# Revit family: Cortadora_CA-31_1_GENERADO
name_source: partatom
category: Equipos especializados
revit_build: Autodesk Revit 2014 (Build: 20131024_2115(x64)
units: mm (PartAtom-declared; Revit-internal decimal feet)

## types (7) — shared parameters
Depth = 405 mm  [stored 1.32874 ft]
Fabricante = SAMMIC S.L.
Foodservice Equipment Identifier = Sí
Height = 544 mm  [stored 1.78478 ft]
Revision Code = 1
Specification by Manufacturer = Single-speed motor block + Regular hopper.
URL = https://www.sammic.com
URL Cutsheet = http://www.sammic.com
Weight in Pounds = 46.3
Width = 389 mm  [stored 1.27625 ft]

## per-type parameters (varying)
| type | Comentarios de tipo | Cycle | Electric Connection Type | FL Amps | Modelo | Phase | Volts |
| Vegetable preparation machine CA-31 230-400/50/3N | Vegetable preparation machine. Production up to 450 kg/hour.

ELECTRICAL DATA:

230V/50Hz/3~ (2.1A) | 50 Hz |  | 1 A | 1050701 | 3 | 400 V |
| Vegetable preparation machine CA-31 230/50/1 | Vegetable preparation machine. Production up to 450 kg/hour. | 50 Hz |  | 5 A | 1050712 | 1 | 230 V |
| Vegetable preparation machine CA-31 120/60/1 | Vegetable preparation machine. Production up to 450 kg/hour. | 60 Hz | USA | 4 A | 1050702 | 1 | 120 V |
| Vegetable preparation machine CA-31 220/60/1 | Vegetable preparation machine. Production up to 450 kg/hour. | 60 Hz | EU | 3 A | 1050705 | 1 | 220 V |
| Vegetable preparation machine CA-31 220/60/1 KSA | Vegetable preparation machine. Production up to 450 kg/hour. | 60 Hz |  | 3 A | 1050706 | 1 | 220 V |
| Vegetable preparation machine CA-31 220-380/60/3N | Vegetable preparation machine. Production up to 450 kg/hour.

ELECTRICAL DATA:

380V/60Hz/3N~ (1.5A) | 60 Hz |  | 2 A | 1050707 | 3 | 220 V |
| Vegetable preparation machine CA-31 230/50/1 AUS | Vegetable preparation machine. Production up to 450 kg/hour. | 50 Hz | AU/NZ | 5 A | 1050708 | 1 | 230 V |

note: column(s) folded — value = type name in every type: Descripción

note: [stored X ft] marks values corroborated as IEEE doubles in the binary element streams (Revit-internal decimal feet)
